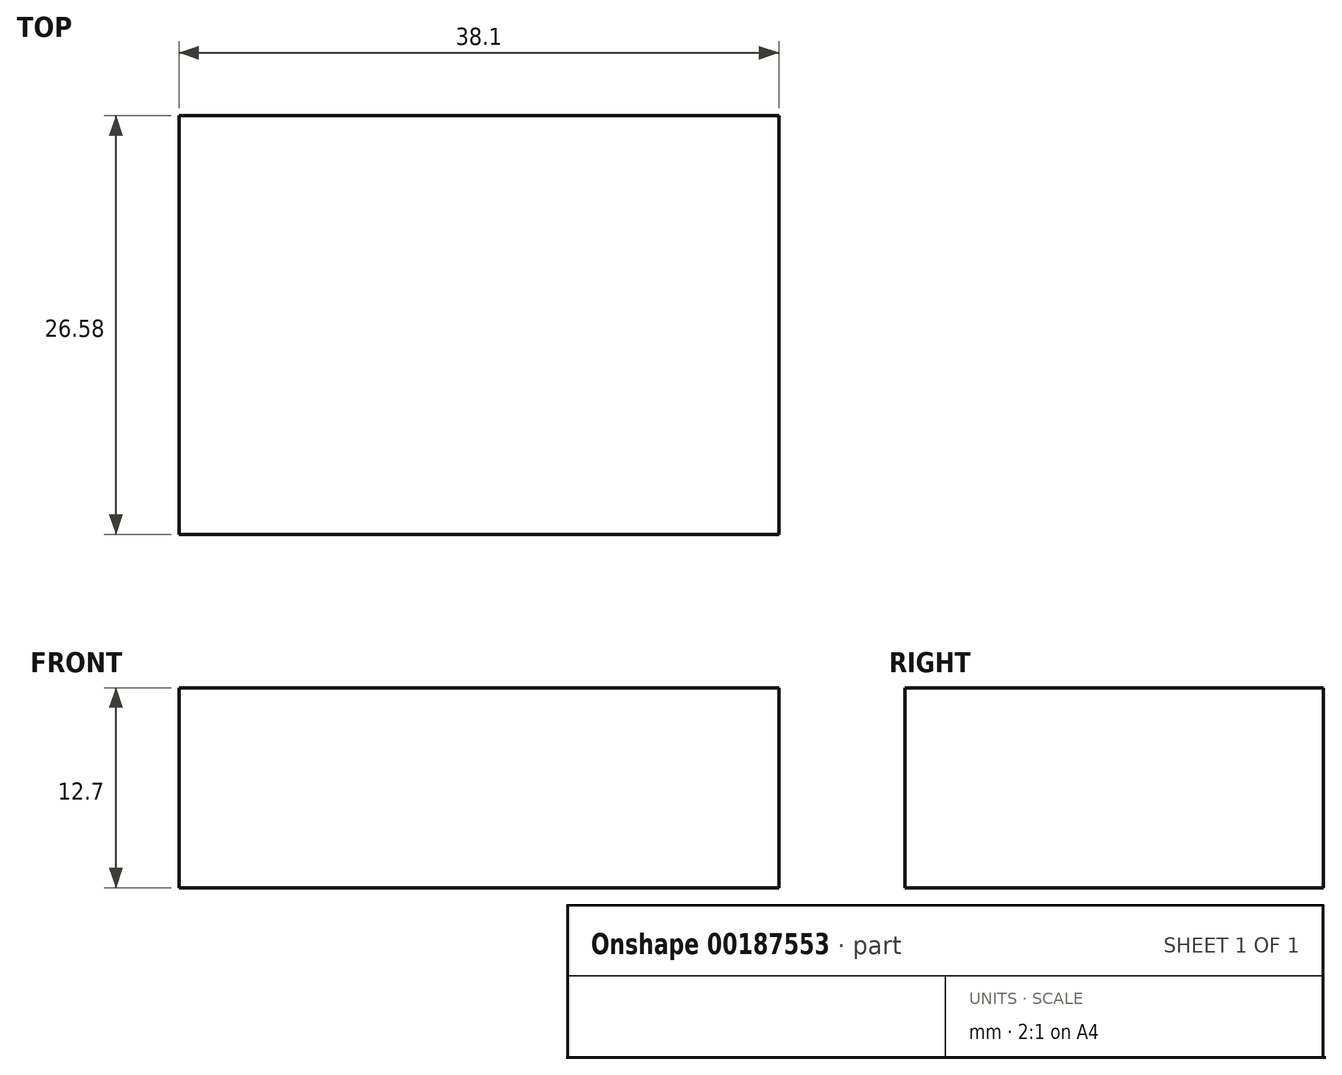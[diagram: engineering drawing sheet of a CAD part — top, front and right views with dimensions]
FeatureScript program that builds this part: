
annotation { "Feature Type Name" : "Feature", "Feature Type Description" : "" }
export const myFeature = defineFeature(function(context is Context, id is Id, definition is map)
    precondition{}
    {
        {
            var Q0;
            Q0=qCreatedBy(makeId("Top.planeOp"),FACE);
            var sketch = newSketch(context, id + "F0", { "sketchPlane" : qUnion([Q0])});
            skLineSegment(sketch, "E0.bottom", {"start": v(-19.05, 13.29) * mm, "end": v(19.05, 13.29) * mm});
            skLineSegment(sketch, "E0.top", {"start": v(-19.05, -13.29) * mm, "end": v(19.05, -13.29) * mm});
            skLineSegment(sketch, "E0.left", {"start": v(-19.05, 13.29) * mm, "end": v(-19.05, -13.29) * mm});
            skLineSegment(sketch, "E0.right", {"start": v(19.05, 13.29) * mm, "end": v(19.05, -13.29) * mm});
            skPoint(sketch, "E0.middle", {"position": v(0, 0) * mm});
            skSolve(sketch);
        }
        {
            var Q0;
            Q0 = qSketchRegion(id + "F0", true);
            extrude(context, id + "F1", {"entities" : qUnion([Q0]), "depth" : 12.7 * mm});
        }
    });
